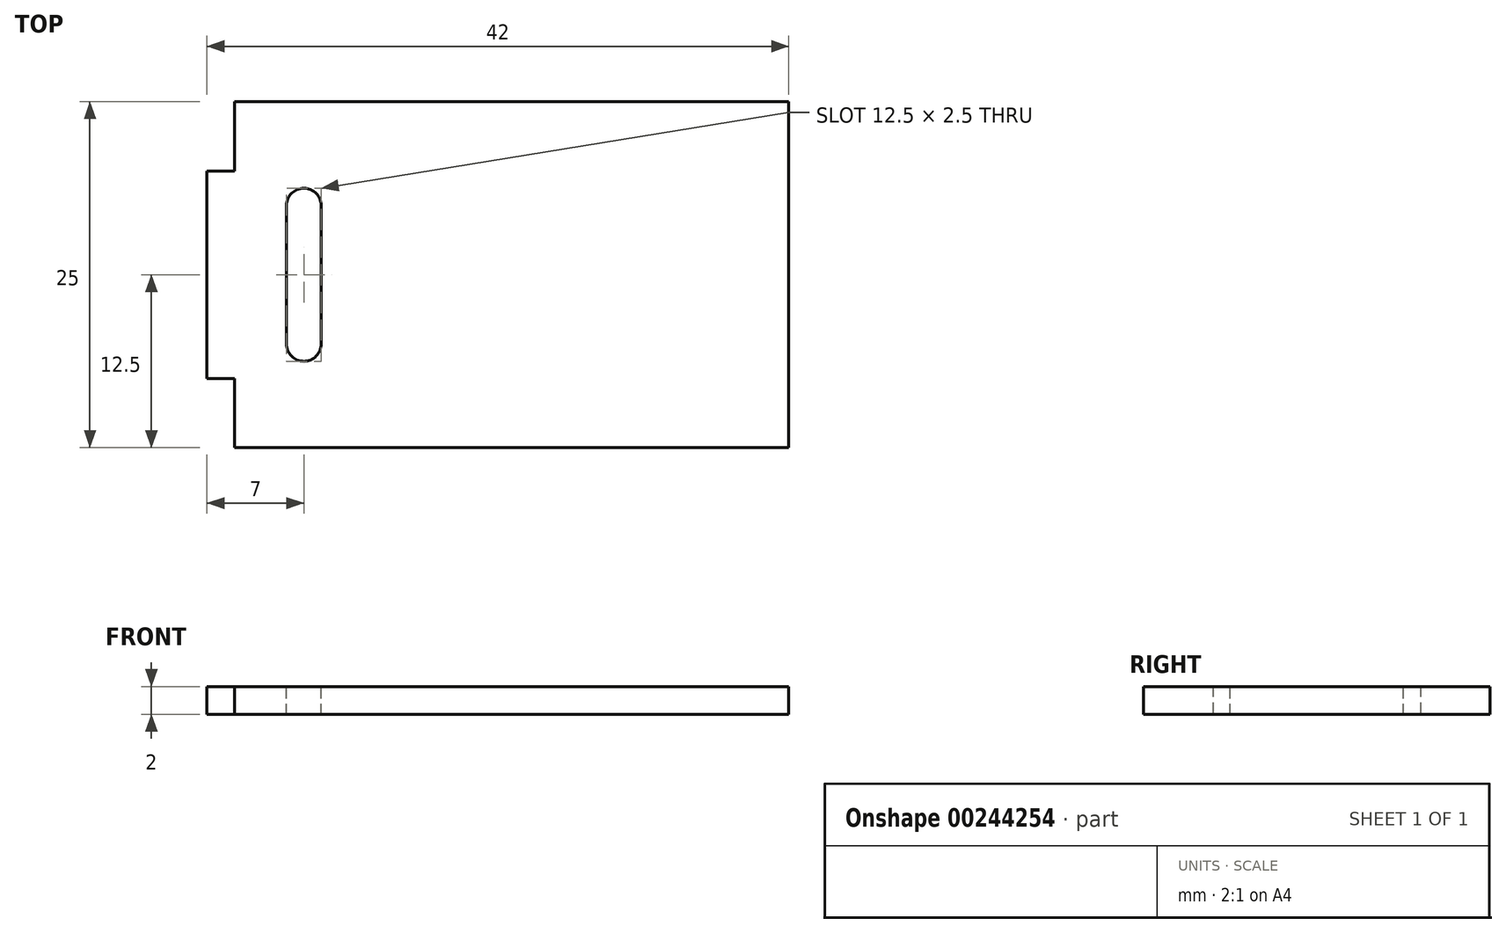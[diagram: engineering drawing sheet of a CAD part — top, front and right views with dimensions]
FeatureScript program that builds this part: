
annotation { "Feature Type Name" : "Feature", "Feature Type Description" : "" }
export const myFeature = defineFeature(function(context is Context, id is Id, definition is map)
    precondition{}
    {
        {
            var Q0;
            Q0=qCreatedBy(makeId("Top.planeOp"),FACE);
            var sketch = newSketch(context, id + "F0", { "sketchPlane" : qUnion([Q0])});
            skLineSegment(sketch, "E0.bottom", {"start": v(20, 12.5) * mm, "end": v(-20, 12.5) * mm});
            skLineSegment(sketch, "E0.top", {"start": v(20, -12.5) * mm, "end": v(-20, -12.5) * mm});
            skLineSegment(sketch, "E0.left", {"start": v(20, 12.5) * mm, "end": v(20, -12.5) * mm});
            skLineSegment(sketch, "E0.right", {"start": v(-20, 12.5) * mm, "end": v(-20, -12.5) * mm});
            skPoint(sketch, "E0.middle", {"position": v(0, 0) * mm});
            skSolve(sketch);
        }
        {
            var Q0;
            Q0=qSketchRegion(id+"F0",true);
            extrude(context, id + "F1", {"entities" : qUnion([Q0]), "depth" : 2 * mm});
        }
        {
            var Q0;
            Q0=qCreatedBy(makeId("Top.planeOp"),FACE);
            var sketch = newSketch(context, id + "F2", { "sketchPlane" : qUnion([Q0])});
            skLineSegment(sketch, "E1", {"start": v(0, 0) * mm, "end": v(-20, 0) * mm, "construction": true});
            skLineSegment(sketch, "E2.bottom", {"start": v(-20, 7.5) * mm, "end": v(-22, 7.5) * mm});
            skLineSegment(sketch, "E2.top", {"start": v(-20, -7.5) * mm, "end": v(-22, -7.5) * mm});
            skLineSegment(sketch, "E2.left", {"start": v(-20, 7.5) * mm, "end": v(-20, -7.5) * mm});
            skLineSegment(sketch, "E2.right", {"start": v(-22, 7.5) * mm, "end": v(-22, -7.5) * mm});
            skSolve(sketch);
        }
        {
            var Q0;
            Q0=qSketchRegion(id+"F2",true);
            extrude(context, id + "F3", {"entities" : qUnion([Q0]), "operationType" : NewBodyOperationType.ADD, "depth" : 2 * mm});
        }
        {
            var Q0;
            {var subQ0=sQuery(id+"F2.wireOp",EDGE,"E2.right");var subQ1=sQuery(id+"F2.wireOp",EDGE,"E2.left");var subQ2=sQuery(id+"F2.wireOp",EDGE,"E2.top");var subQ3=sQuery(id+"F2.wireOp",EDGE,"E2.bottom");Q0=makeQuery(id+"FaRhJeDl5bXZvjD_1.1.F3.boolean.opBoolean","MERGE",FACE,{"derivedFrom":[makeQuery(id+"F3.boolean.opBoolean","MERGE",FACE,{"derivedFrom":[makeQuery(id+"F1.opExtrude","CAP_FACE",FACE,{"disambiguationData":[OSD([sQuery(id+"F0.wireOp",EDGE,"E0.bottom"),sQuery(id+"F0.wireOp",EDGE,"E0.top"),sQuery(id+"F0.wireOp",EDGE,"E0.left"),sQuery(id+"F0.wireOp",EDGE,"E0.right")])],"isStart":false}),makeQuery(id+"F3.opExtrude","CAP_FACE",FACE,{"disambiguationData":[OSD([subQ3,subQ2,subQ1,subQ0])],"isStart":false})]}),makeQuery(id+"FaRhJeDl5bXZvjD_1.1.F3.opExtrude","CAP_FACE",FACE,{"disambiguationData":[OSD([subQ3,subQ2,subQ1,subQ0])],"isStart":false})]});}
            var sketch = newSketch(context, id + "F4", { "sketchPlane" : qUnion([Q0])});
            skLineSegment(sketch, "E3", {"start": v(0, 0) * mm, "end": v(-15, 0) * mm, "construction": true});
            skLineSegment(sketch, "E4", {"start": v(-15, 5) * mm, "end": v(-15, -5) * mm, "construction": true});
            skArc(sketch, "E5.0.startCap", {"start": v(-16.25, 5) * mm, "mid": v(-15, 6.25) * mm, "end": v(-13.75, 5) * mm});
            skArc(sketch, "E5.0.endCap", {"start": v(-13.75, -5) * mm, "mid": v(-15, -6.25) * mm, "end": v(-16.25, -5) * mm});
            skLineSegment(sketch, "E5.0.left", {"start": v(-13.75, 5) * mm, "end": v(-13.75, -5) * mm});
            skLineSegment(sketch, "E5.0.right", {"start": v(-16.25, 5) * mm, "end": v(-16.25, -5) * mm});
            skSolve(sketch);
        }
        {
            var Q0;
            Q0=qSketchRegion(id+"F4",true);
            extrude(context, id + "F5", {"entities" : qUnion([Q0]), "operationType" : NewBodyOperationType.REMOVE, "endBound" : BoundingType.THROUGH_ALL, "oppositeDirection" : true, "depth" : 25 * mm});
        }
    });
